# Revit family: Reece_Vanity_Roca_Ona_Centre Bowl_1000 mm
name_source: partatom
category: Casework
revit_build: Autodesk Revit 2018 (Build: 20181011_1500(x64)
units: mm (PartAtom-declared; Revit-internal decimal feet)

## family parameters
Always vertical = Yes
Cut with Voids When Loaded = Yes
Room Calculation Point = Yes
Shared = Yes
Work Plane-Based = Yes

## types (1)
- Reece_Vanity_Roca_Ona_Centre Bowl_1000 mm
    Construction Type = Vanity
    Default Elevation = 0 mm  [stored 0 ft]
    Disclaimer = THIS FILE IS THE PROPERTY OF THE REECE GROUP. IT MAY NOT BE REPRODUCED, REVERSE-ENGINEERED, OR MODIFIED. ANY REPUBLICATION, TRANSMISSION, OR DISTRIBUTION FOR THE PURPOSE OF COMMERCIALLY EXPLOITING THE FILES IS PROHIBITED.
    Reece_Basin_Outlet = 46 mm  [stored 0.150919 ft]
    Reece_Cabinet_Depth = 450 mm  [stored 1.47638 ft]
    Reece_Casework_Type = 1
    Reece_Cut_Type = 0
    Reece_Detail_Additional = Please refer to Colour, Finish and Material Variations Document for more information.
    Reece_Detail_Disclaimer = THIS FILE IS THE PROPERTY OF THE REECE GROUP. IT MAY NOT BE REPRODUCED, REVERSE-ENGINEERED, OR MODIFIED. ANY REPUBLICATION, TRANSMISSION, OR DISTRIBUTION FOR THE PURPOSE OF COMMERCIALLY EXPLOITING THE FILES IS PROHIBITED.
    Reece_Material_Benchtop = Reece_FINECERAMIC_White
    Reece_Material_Cabinet = Reece_Timber_Dark Elm
    Reece_Material_Colour = Reece_Polyurethane_Matte Grey
    Reece_Material_Main = Reece_Timber_Dark Elm_Vertical
    Reece_Material_Secondary = Reece_Brass_Chrome
    Reece_Overall_Capacity = 8.7 L
    Reece_Overall_Depth = 460 mm  [stored 1.50919 ft]
    Reece_Overall_Height = 645 mm  [stored 2.11614 ft]
    Reece_Overall_Width = 1000 mm  [stored 3.28084 ft]
    Reece_Product_Brand = Roca
    Reece_Product_Mount = Wall Mounted
    Reece_Product_Sub Brand = Ona
    Reece_Product_Type = Vanity

note: [stored X ft] marks values corroborated as IEEE doubles in the binary element streams (Revit-internal decimal feet)

## geometry (parser evidence)
native form markers: Sweep x8
no freeform markers — native parametric forms only
